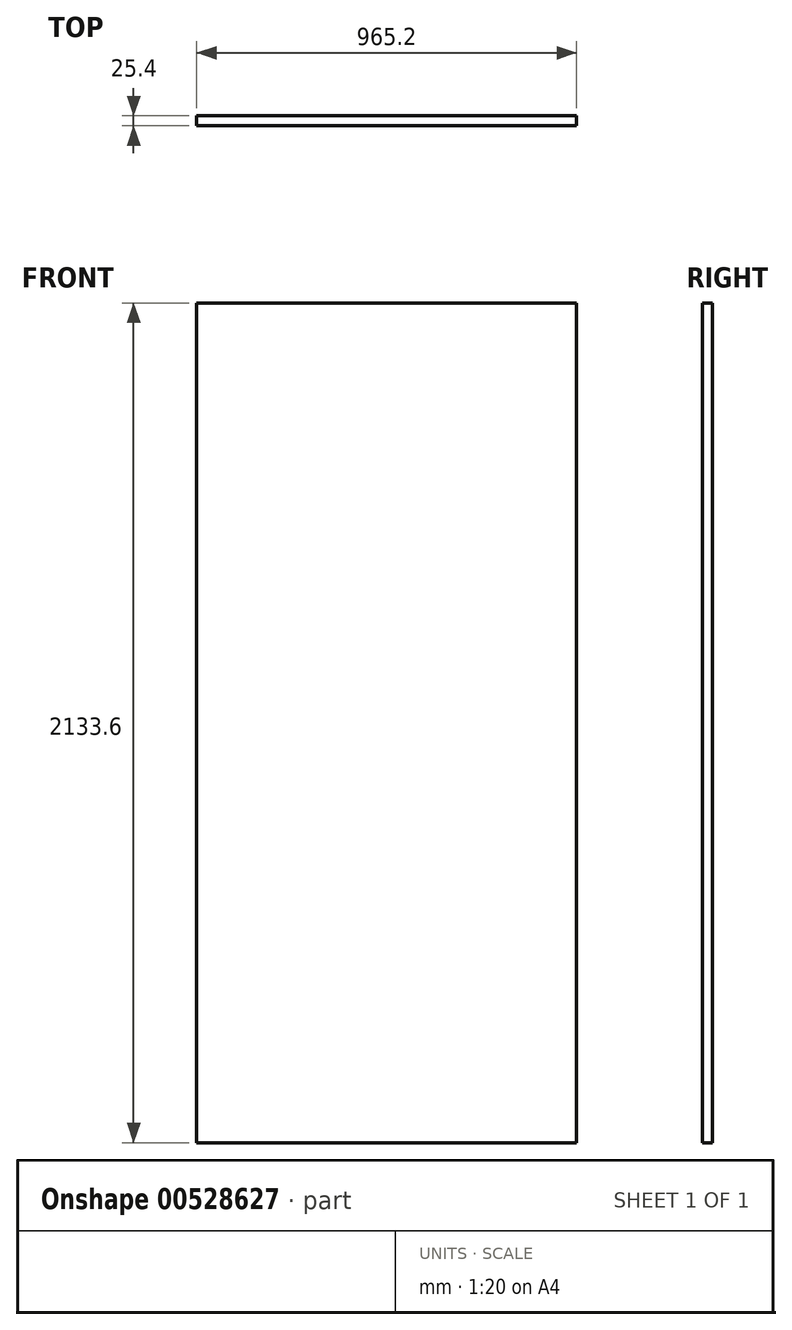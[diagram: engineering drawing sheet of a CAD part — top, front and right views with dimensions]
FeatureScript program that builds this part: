
annotation { "Feature Type Name" : "Feature", "Feature Type Description" : "" }
export const myFeature = defineFeature(function(context is Context, id is Id, definition is map)
    precondition{}
    {
        {
            var Q0;
            Q0=qCreatedBy(makeId("Front.planeOp"),FACE);
            var sketch = newSketch(context, id + "F0", { "sketchPlane" : qUnion([Q0])});
            skLineSegment(sketch, "E0.bottom", {"start": v(482.6, -1066.8) * mm, "end": v(0, -1066.8) * mm});
            skLineSegment(sketch, "E0.top", {"start": v(482.6, 1066.8) * mm, "end": v(0, 1066.8) * mm});
            skLineSegment(sketch, "E0.left", {"start": v(482.6, -1066.8) * mm, "end": v(482.6, 1066.8) * mm});
            skLineSegment(sketch, "E0.right", {"start": v(-482.6, -1066.8) * mm, "end": v(-482.6, 1066.8) * mm});
            skPoint(sketch, "E0.middle", {"position": v(0, 0) * mm});
            skLineSegment(sketch, "E1", {"start": v(0, 1066.8) * mm, "end": v(-482.6, 1066.8) * mm});
            skLineSegment(sketch, "E2", {"start": v(0, -1066.8) * mm, "end": v(-482.6, -1066.8) * mm});
            skLineSegment(sketch, "E3", {"start": v(0, 1066.8) * mm, "end": v(0, -1066.8) * mm});
            skLineSegment(sketch, "E4", {"start": v(0, 1066.8) * mm, "end": v(-482.6, 584.2) * mm});
            skLineSegment(sketch, "E5.1.0.0", {"start": v(0, 923.04) * mm, "end": v(-482.6, 440.44) * mm});
            skLineSegment(sketch, "E5.2.0.0", {"start": v(0, 779.27) * mm, "end": v(-482.6, 296.67) * mm});
            skLineSegment(sketch, "E5.3.0.0", {"start": v(0, 635.5) * mm, "end": v(-482.6, 152.9) * mm});
            skLineSegment(sketch, "E5.4.0.0", {"start": v(0, 491.74) * mm, "end": v(-482.6, 9.14) * mm});
            skLineSegment(sketch, "E5.5.0.0", {"start": v(0, 347.98) * mm, "end": v(-482.6, -134.62) * mm});
            skLineSegment(sketch, "E5.6.0.0", {"start": v(0, 204.22) * mm, "end": v(-482.6, -278.38) * mm});
            skLineSegment(sketch, "E5.7.0.0", {"start": v(0, 60.45) * mm, "end": v(-482.6, -422.15) * mm});
            skLineSegment(sketch, "E5.8.0.0", {"start": v(0, -83.31) * mm, "end": v(-482.6, -565.91) * mm});
            skLineSegment(sketch, "E5.9.0.0", {"start": v(0, -227.08) * mm, "end": v(-482.6, -709.68) * mm});
            skLineSegment(sketch, "E5.10.0.0", {"start": v(0, -370.84) * mm, "end": v(-482.6, -853.44) * mm});
            skLineSegment(sketch, "E5.11.0.0", {"start": v(0, -514.6) * mm, "end": v(-482.6, -997.2) * mm});
            skLineSegment(sketch, "E5.12.0.0", {"start": v(0, -658.37) * mm, "end": v(-408.43, -1066.8) * mm});
            skLineSegment(sketch, "E5.13.0.0", {"start": v(0, -802.13) * mm, "end": v(-264.67, -1066.8) * mm});
            skLineSegment(sketch, "E5.14.0.0", {"start": v(0, -945.9) * mm, "end": v(-120.9, -1066.8) * mm});
            skLineSegment(sketch, "E5.direction1", {"start": v(-482.6, 584.2) * mm, "end": v(-482.6, 440.44) * mm, "construction": true});
            skPoint(sketch, "E6.orphan", {"position": v(-482.6, -1428.5) * mm});
            skPoint(sketch, "E7.orphan", {"position": v(-482.6, -1284.73) * mm});
            skPoint(sketch, "E8.orphan", {"position": v(-482.6, -1140.97) * mm});
            skLineSegment(sketch, "E9.1.0.0", {"start": v(-143.76, 1066.8) * mm, "end": v(-482.6, 727.96) * mm});
            skLineSegment(sketch, "E9.2.0.0", {"start": v(-287.53, 1066.8) * mm, "end": v(-482.6, 871.73) * mm});
            skLineSegment(sketch, "E9.3.0.0", {"start": v(-431.3, 1066.8) * mm, "end": v(-482.6, 1015.5) * mm});
            skLineSegment(sketch, "E9.direction1", {"start": v(-482.6, 584.2) * mm, "end": v(-626.36, 584.2) * mm, "construction": true});
            skPoint(sketch, "E10.orphan", {"position": v(-913.9, 584.2) * mm});
            skPoint(sketch, "E11.orphan", {"position": v(-770.13, 584.2) * mm});
            skLineSegment(sketch, "E12", {"start": v(0, 1066.8) * mm, "end": v(482.6, 584.2) * mm});
            skLineSegment(sketch, "E13.1.0.0", {"start": v(143.76, 1066.8) * mm, "end": v(482.6, 727.96) * mm});
            skLineSegment(sketch, "E13.2.0.0", {"start": v(287.53, 1066.8) * mm, "end": v(482.6, 871.73) * mm});
            skLineSegment(sketch, "E13.3.0.0", {"start": v(431.3, 1066.8) * mm, "end": v(482.6, 1015.5) * mm});
            skLineSegment(sketch, "E13.direction1", {"start": v(0, 1066.8) * mm, "end": v(143.76, 1066.8) * mm, "construction": true});
            skPoint(sketch, "E14.orphan", {"position": v(913.9, 584.2) * mm});
            skPoint(sketch, "E15.orphan", {"position": v(770.13, 584.2) * mm});
            skPoint(sketch, "E16.orphan", {"position": v(626.36, 584.2) * mm});
            skLineSegment(sketch, "E17.1.0.0", {"start": v(0, 923.04) * mm, "end": v(482.6, 440.44) * mm});
            skLineSegment(sketch, "E17.2.0.0", {"start": v(0, 779.27) * mm, "end": v(482.6, 296.67) * mm});
            skLineSegment(sketch, "E17.3.0.0", {"start": v(0, 635.5) * mm, "end": v(482.6, 152.9) * mm});
            skLineSegment(sketch, "E17.4.0.0", {"start": v(0, 491.74) * mm, "end": v(482.6, 9.14) * mm});
            skLineSegment(sketch, "E17.5.0.0", {"start": v(0, 347.98) * mm, "end": v(482.6, -134.62) * mm});
            skLineSegment(sketch, "E17.6.0.0", {"start": v(0, 204.22) * mm, "end": v(482.6, -278.38) * mm});
            skLineSegment(sketch, "E17.7.0.0", {"start": v(0, 60.45) * mm, "end": v(482.6, -422.15) * mm});
            skLineSegment(sketch, "E17.8.0.0", {"start": v(0, -83.31) * mm, "end": v(482.6, -565.91) * mm});
            skLineSegment(sketch, "E17.9.0.0", {"start": v(0, -227.08) * mm, "end": v(482.6, -709.68) * mm});
            skLineSegment(sketch, "E17.10.0.0", {"start": v(0, -370.84) * mm, "end": v(482.6, -853.44) * mm});
            skLineSegment(sketch, "E17.11.0.0", {"start": v(0, -514.6) * mm, "end": v(482.6, -997.2) * mm});
            skLineSegment(sketch, "E17.12.0.0", {"start": v(0, -658.37) * mm, "end": v(408.43, -1066.8) * mm});
            skLineSegment(sketch, "E17.13.0.0", {"start": v(0, -802.13) * mm, "end": v(264.67, -1066.8) * mm});
            skLineSegment(sketch, "E17.14.0.0", {"start": v(0, -945.9) * mm, "end": v(120.9, -1066.8) * mm});
            skLineSegment(sketch, "E17.direction1", {"start": v(0, 1066.8) * mm, "end": v(0, 923.04) * mm, "construction": true});
            skPoint(sketch, "E18.orphan", {"position": v(482.6, -1428.5) * mm});
            skPoint(sketch, "E19.orphan", {"position": v(482.6, -1284.73) * mm});
            skPoint(sketch, "E20.orphan", {"position": v(482.6, -1140.97) * mm});
            skSolve(sketch);
        }
        {
            var Q0;
            Q0 = qSketchRegion(id + "F0", true);
            extrude(context, id + "F1", {"entities" : qUnion([Q0]), "endBound" : BoundingType.SYMMETRIC, "oppositeDirection" : true, "depth" : 25.4 * mm, "offsetDistance" : 25.4 * mm, "hasSecondDirection" : true, "secondDirectionOppositeDirection" : true, "secondDirectionDepth" : 25.4 * mm});
        }
    });
